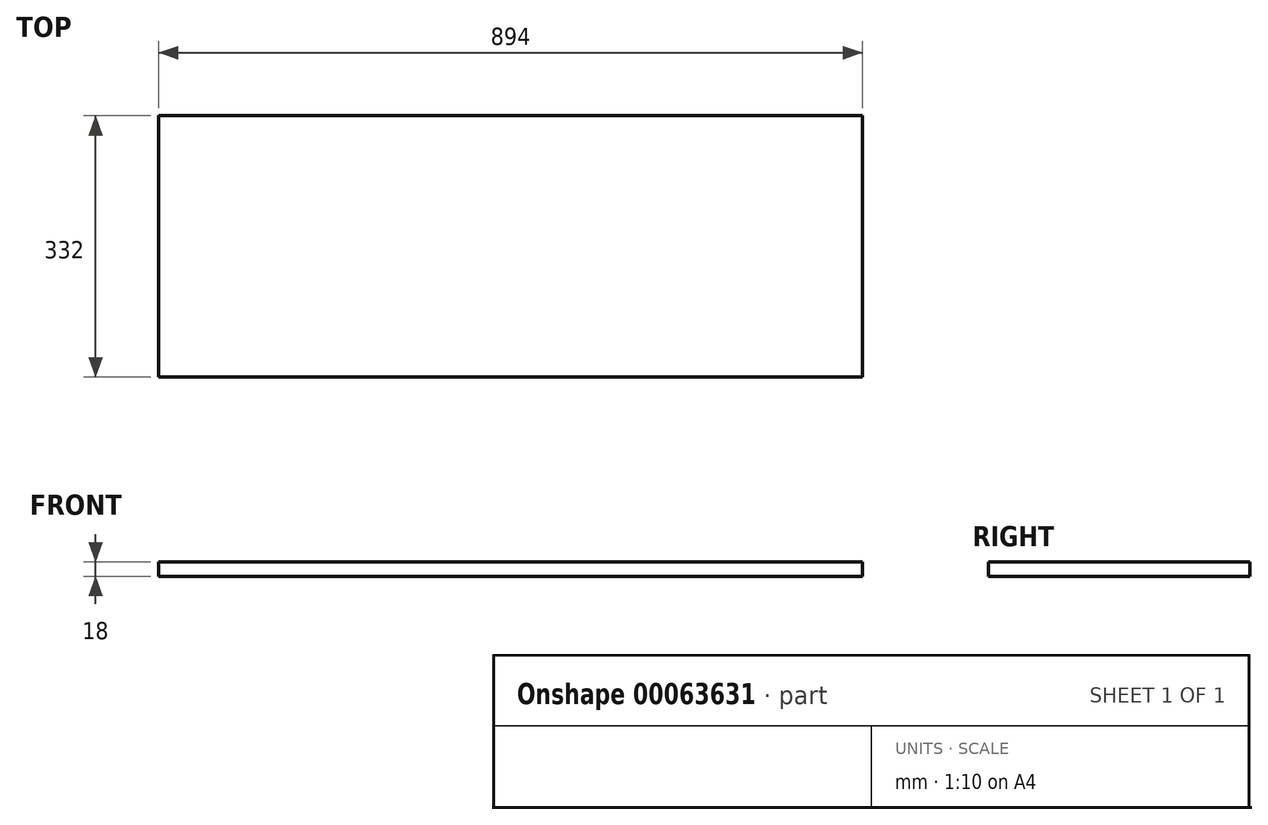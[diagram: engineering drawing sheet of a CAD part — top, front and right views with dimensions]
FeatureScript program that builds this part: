
annotation { "Feature Type Name" : "Feature", "Feature Type Description" : "" }
export const myFeature = defineFeature(function(context is Context, id is Id, definition is map)
    precondition{}
    {
        {
            var Q0;
            Q0=qCreatedBy(makeId("Top.planeOp"),FACE);
            var sketch = newSketch(context, id + "F0", { "sketchPlane" : qUnion([Q0])});
            skLineSegment(sketch, "E0.bottom", {"start": v(0, 0) * mm, "end": v(894, 0) * mm});
            skLineSegment(sketch, "E0.top", {"start": v(0, -332) * mm, "end": v(894, -332) * mm});
            skLineSegment(sketch, "E0.left", {"start": v(0, 0) * mm, "end": v(0, -332) * mm});
            skLineSegment(sketch, "E0.right", {"start": v(894, 0) * mm, "end": v(894, -332) * mm});
            skSolve(sketch);
        }
        {
            var Q0;
            Q0 = qSketchRegion(id + "F0", true);
            extrude(context, id + "F1", {"entities" : qUnion([Q0]), "depth" : 18 * mm});
        }
    });
